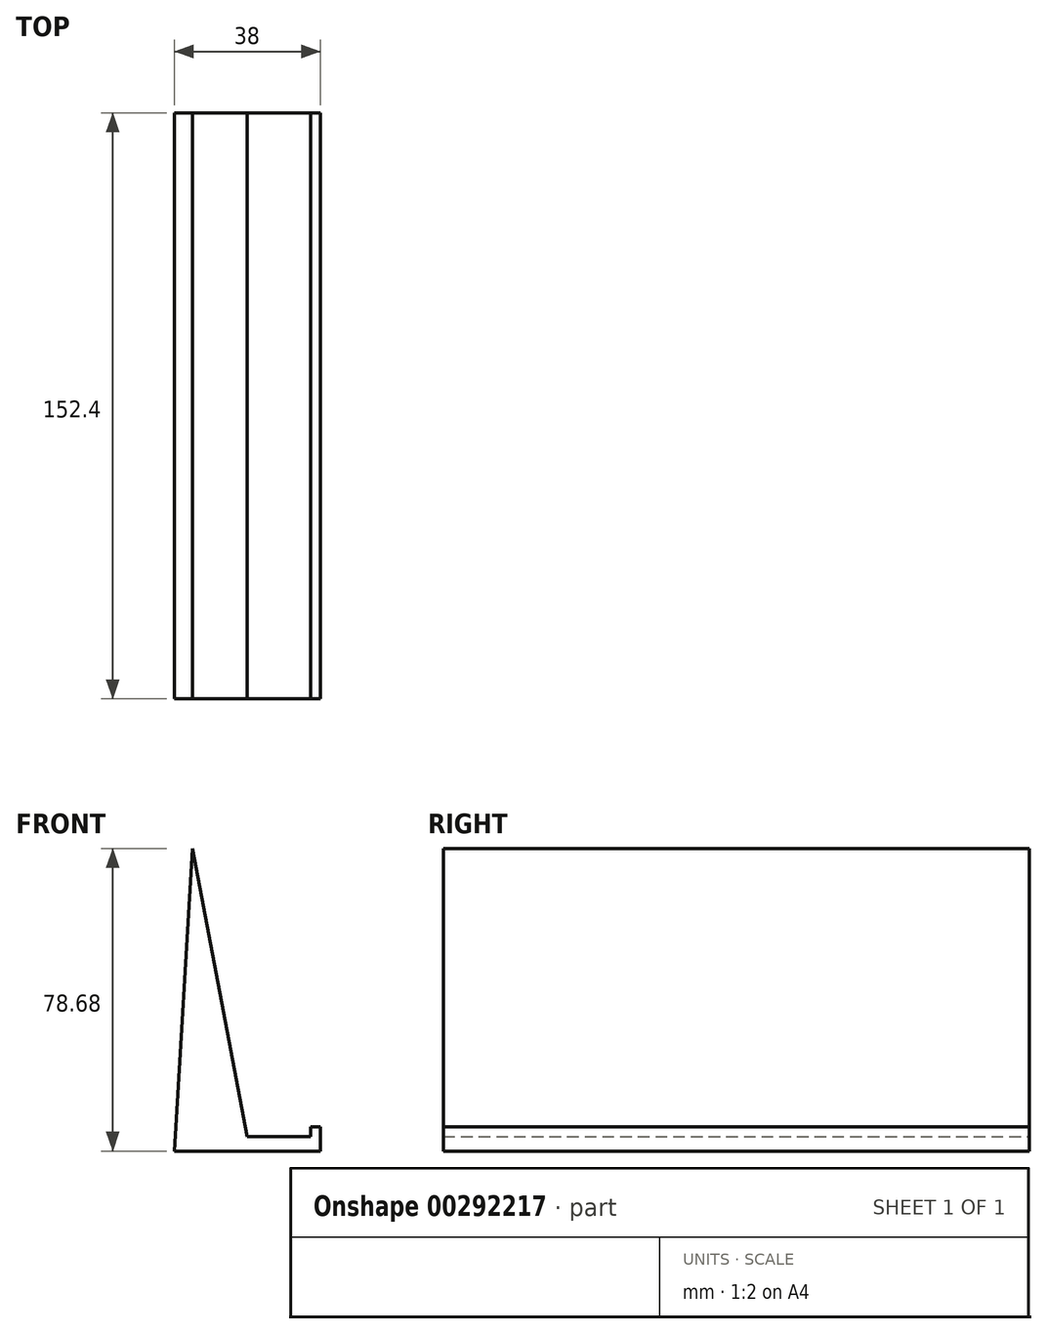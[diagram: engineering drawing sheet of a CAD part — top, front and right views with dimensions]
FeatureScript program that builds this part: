
annotation { "Feature Type Name" : "Feature", "Feature Type Description" : "" }
export const myFeature = defineFeature(function(context is Context, id is Id, definition is map)
    precondition{}
    {
        {
            var Q0;
            Q0=qCreatedBy(makeId("Front.planeOp"),FACE);
            var sketch = newSketch(context, id + "F0", { "sketchPlane" : qUnion([Q0])});
            skLineSegment(sketch, "E0", {"start": v(0, 0) * mm, "end": v(0, 6.35) * mm});
            skPoint(sketch, "E1.end.orphan", {"position": v(-17.78, 34.75) * mm});
            skLineSegment(sketch, "E2", {"start": v(0, 6.35) * mm, "end": v(-2.54, 6.35) * mm});
            skLineSegment(sketch, "E3", {"start": v(-2.54, 6.35) * mm, "end": v(-2.54, 3.81) * mm});
            skLineSegment(sketch, "E4", {"start": v(-2.54, 3.81) * mm, "end": v(-19.05, 3.81) * mm});
            skLineSegment(sketch, "E5", {"start": v(-19.05, 3.81) * mm, "end": v(-33.22, 78.68) * mm});
            skLineSegment(sketch, "E6", {"start": v(-33.22, 78.68) * mm, "end": v(-38, 0) * mm});
            skPoint(sketch, "E7.end.orphan", {"position": v(-31.75, 0) * mm});
            skLineSegment(sketch, "E8", {"start": v(0, 0) * mm, "end": v(-38, 0) * mm});
            skSolve(sketch);
        }
        {
            var Q0;
            Q0 = qSketchRegion(id + "F0", true);
            extrude(context, id + "F1", {"entities" : qUnion([Q0]), "depth" : 152.4 * mm});
        }
    });
